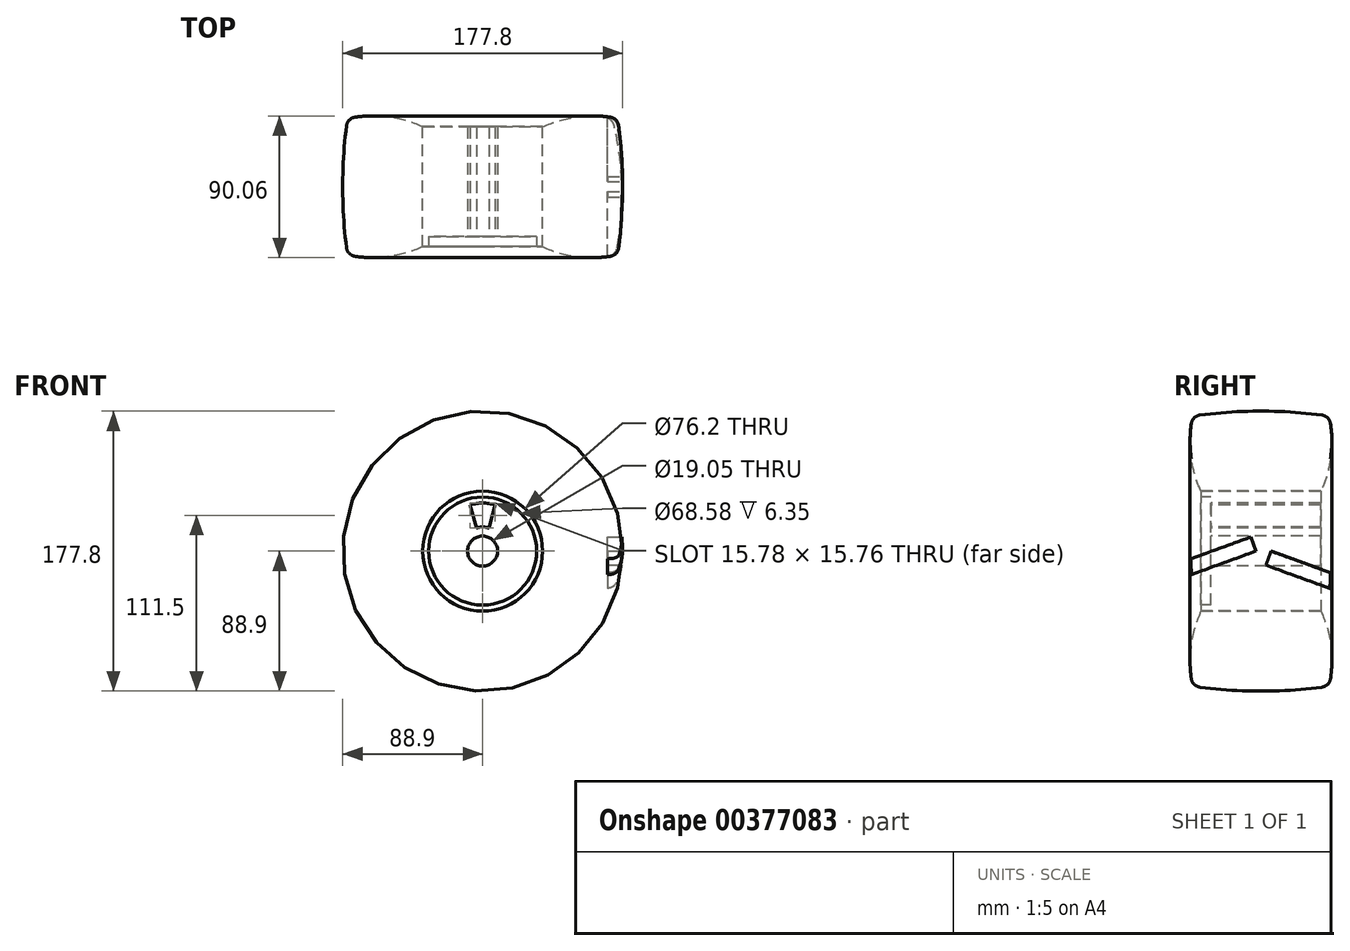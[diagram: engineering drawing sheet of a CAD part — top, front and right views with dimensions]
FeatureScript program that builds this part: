
annotation { "Feature Type Name" : "Feature", "Feature Type Description" : "" }
export const myFeature = defineFeature(function(context is Context, id is Id, definition is map)
    precondition{}
    {
        {
            var Q0;
            Q0=qCreatedBy(makeId("Front.planeOp"),FACE);
            var sketch = newSketch(context, id + "F0", { "sketchPlane" : qUnion([Q0])});
            skCircle(sketch, "E0", {"center": v(0, 0) * mm, "radius": 38.1 * mm});
            skCircle(sketch, "E1", {"center": v(0, 0) * mm, "radius": 9.53 * mm});
            skSolve(sketch);
        }
        {
            var Q0;
            Q0 = qSketchRegion(id + "F0", true);
            extrude(context, id + "F1", {"entities" : qUnion([Q0]), "endBound" : BoundingType.SYMMETRIC, "oppositeDirection" : true, "depth" : 76.2 * mm});
        }
        {
            var Q0;
            Q0=makeQuery(id+"F1.opExtrude","CAP_FACE",FACE,{"disambiguationData":[OSD([sQuery(id+"F0.wireOp",EDGE,"E0")])],"isStart":true});
            var sketch = newSketch(context, id + "F2", { "sketchPlane" : qUnion([Q0])});
            skArc(sketch, "E2", {"start": v(3.94, 14.72) * mm, "mid": v(0, 15.24) * mm, "end": v(-3.94, 14.72) * mm});
            skArc(sketch, "E3", {"start": v(7.89, 29.44) * mm, "mid": v(0, 30.48) * mm, "end": v(-7.89, 29.44) * mm});
            skLineSegment(sketch, "E4", {"start": v(0, 0) * mm, "end": v(0, 30.48) * mm, "construction": true});
            skLineSegment(sketch, "E5", {"start": v(-3.94, 14.72) * mm, "end": v(-7.89, 29.44) * mm});
            skLineSegment(sketch, "E6.MirrorCS", {"start": v(3.94, 14.72) * mm, "end": v(7.89, 29.44) * mm});
            skLineSegment(sketch, "E7", {"start": v(3.94, 14.72) * mm, "end": v(0, 0) * mm, "construction": true});
            skLineSegment(sketch, "E8", {"start": v(0, 0) * mm, "end": v(-3.94, 14.72) * mm, "construction": true});
            skSolve(sketch);
        }
        {
            var Q0;
            Q0 = qSketchRegion(id + "F2", true);
            extrude(context, id + "F3", {"entities" : qUnion([Q0]), "operationType" : NewBodyOperationType.REMOVE, "endBound" : BoundingType.THROUGH_ALL, "oppositeDirection" : true, "depth" : 25.4 * mm});
        }
        {
            var Q0;
            Q0=makeQuery(id+"F1.opExtrude","CAP_FACE",FACE,{"disambiguationData":[OSD([sQuery(id+"F0.wireOp",EDGE,"E0")])],"isStart":true});
            var sketch = newSketch(context, id + "F4", { "sketchPlane" : qUnion([Q0])});
            skCircle(sketch, "E9", {"center": v(0, 0) * mm, "radius": 34.3 * mm});
            skSolve(sketch);
        }
        {
            var Q0;
            Q0 = qSketchRegion(id + "F4", true);
            extrude(context, id + "F5", {"entities" : qUnion([Q0]), "operationType" : NewBodyOperationType.REMOVE, "oppositeDirection" : true, "depth" : 6.35 * mm});
        }
        {
            var Q0;
            Q0=qCreatedBy(makeId("Right.planeOp"),FACE);
            var sketch = newSketch(context, id + "F6", { "sketchPlane" : qUnion([Q0])});
            skLineSegment(sketch, "E10.bottom", {"start": v(-38.1, 38.1) * mm, "end": v(38.1, 38.1) * mm});
            skLineSegment(sketch, "E11", {"start": v(0, 38.1) * mm, "end": v(0, 88.9) * mm, "construction": true});
            skArc(sketch, "E12", {"start": v(0, 88.9) * mm, "mid": v(-19.4, 88.28) * mm, "end": v(-38.73, 86.43) * mm});
            skArc(sketch, "E13", {"start": v(-44.2, 81.07) * mm, "mid": v(-44.27, 59.14) * mm, "end": v(-38.1, 38.1) * mm});
            skPoint(sketch, "E14.visualSharp", {"position": v(-43.34, 85.8) * mm});
            skArc(sketch, "E14.filletArc", {"start": v(-38.73, 86.43) * mm, "mid": v(-42.36, 84.67) * mm, "end": v(-44.2, 81.07) * mm});
            skArc(sketch, "E15.MirrorCS", {"start": v(44.2, 81.07) * mm, "mid": v(44.27, 59.14) * mm, "end": v(38.1, 38.1) * mm});
            skArc(sketch, "E16.MirrorCS", {"start": v(38.73, 86.43) * mm, "mid": v(42.36, 84.67) * mm, "end": v(44.2, 81.07) * mm});
            skArc(sketch, "E17.MirrorCS", {"start": v(0, 88.9) * mm, "mid": v(19.4, 88.28) * mm, "end": v(38.73, 86.43) * mm});
            skSolve(sketch);
        }
        {
            var Q0;
            Q0=makeQuery(id+"F6.imprint","IMPRINT",FACE,{"disambiguationData":[TD([[makeQuery(id+"F6.imprint","IMPRINT",EDGE,{"derivedFrom":sQuery(id+"F6.wireOp",EDGE,"E10.bottom")}),1.0]])]});
            var Q1;
            Q1=makeQuery(id+"F1.opExtrude","CAP_EDGE",EDGE,{"disambiguationData":[OSD([sQuery(id+"F0.wireOp",EDGE,"E0")])],"isStart":true});
            revolve(context, id + "F7", {"entities" : qUnion([Q0]), "axis" : qUnion([Q1]), "revolveType" : RevolveType.FULL});
        }
        {
            var Q0;
            Q0=qCreatedBy(makeId("Right.planeOp"),FACE);
            cPlane(context, id + "F8", {"entities" : qUnion([Q0]), "cplaneType" : CPlaneType.OFFSET, "offset" : 88.9 * mm, "width" : 152.4 * mm, "height" : 152.4 * mm});
        }
        {
            var Q0;
            Q0=qCreatedBy(id+"F8.planeOp",FACE);
            var sketch = newSketch(context, id + "F9", { "sketchPlane" : qUnion([Q0])});
            skLineSegment(sketch, "E18.bottom", {"start": v(-50.91, -17.37) * mm, "end": v(-3.17, 0) * mm});
            skLineSegment(sketch, "E18.top", {"start": v(-54.17, -8.42) * mm, "end": v(-6.43, 8.95) * mm});
            skLineSegment(sketch, "E18.left", {"start": v(-50.91, -17.37) * mm, "end": v(-54.17, -8.42) * mm});
            skLineSegment(sketch, "E18.right", {"start": v(-3.18, 0) * mm, "end": v(-6.43, 8.95) * mm});
            skLineSegment(sketch, "E19.bottom", {"start": v(6.43, 0) * mm, "end": v(54.17, -17.37) * mm});
            skLineSegment(sketch, "E19.top", {"start": v(3.17, -8.95) * mm, "end": v(50.91, -26.33) * mm});
            skLineSegment(sketch, "E19.left", {"start": v(6.43, 0) * mm, "end": v(3.17, -8.95) * mm});
            skLineSegment(sketch, "E19.right", {"start": v(54.17, -17.37) * mm, "end": v(50.91, -26.33) * mm});
            skSolve(sketch);
        }
        {
            var Q0;
            Q0 = qSketchRegion(id + "F9", true);
            extrude(context, id + "F10", {"entities" : qUnion([Q0]), "operationType" : NewBodyOperationType.REMOVE, "oppositeDirection" : true, "depth" : 9.52 * mm});
        }
    });
